# Revit family: Base_Cabinets-Teknion-CEBDS_Base_Cabinet_Door(s)_And_Drawer(s)-R2022
name_source: partatom
category: Furniture
units: mm (PartAtom-declared; Revit-internal decimal feet)

## family parameters
Always vertical = Yes
Cut with Voids When Loaded = No
Enable Cutting in Views = No
OmniClass Number = 23.40.20.00
OmniClass Title = General Furniture and Specialties
Render Appearance Source = Family Geometry
Room Calculation Point = No
Shared = Yes
Work Plane-Based = No

## types (3) — shared parameters
Assembly Code = E2020200
Manufacturer = Teknion
Manufacturer Fax = 416.661.4586
Part Number = CEBDS
Product Documentation Link = https://www.teknion.com
Product Line = Base Cabinets
Product Page URL = https://www.teknion.com
Series = Expansion Casework+
Sustainability Data = https://www.teknion.com
URL = www.teknion.com
Unit Weight URL = http://www.teknion.com
Warranty = http://www.teknion.com
zero-valued in all types: Default Elevation

## per-type parameters (varying)
| type | 2D - Two Doors | Cut-Out - Front 1 | Cut-Out - Front 2 | Description | Lock - 2 Doors | MR - 1 Handle | MR - 2 Handles | Model | O - One Door & One Drawer | One Drawer | T - Two Doors & One Drawer | Two Drawers | X - Two Doors & Two Drawers |
| One Door & One Drawer Configuration | No | 0.3 " | 0.3 " | Base Cabinet - Door(s) and Drawer(s), One Door & One Drawer Configuration | No | Yes | No | CEBDSO_____ | Yes | Yes | No | No | No |
| Two Doors & One Drawer Configuration | Yes | 0.3 " | 3 " | Base Cabinet - Door(s) and Drawer(s), Two Doors & One Drawer Configuration | Yes | Yes | Yes | CEBDST____ | No | Yes | Yes | No | No |
| Two Doors & Two Drawers Configuration | Yes | 3 " | 3 " | Base Cabinet - Door(s) and Drawer(s), Two Doors & Two Drawers Configuration | Yes | No | Yes | CEBDSX____ | No | No | No | Yes | Yes |

## geometry (parser evidence)
native form markers: Sweep x3
no freeform markers — native parametric forms only
